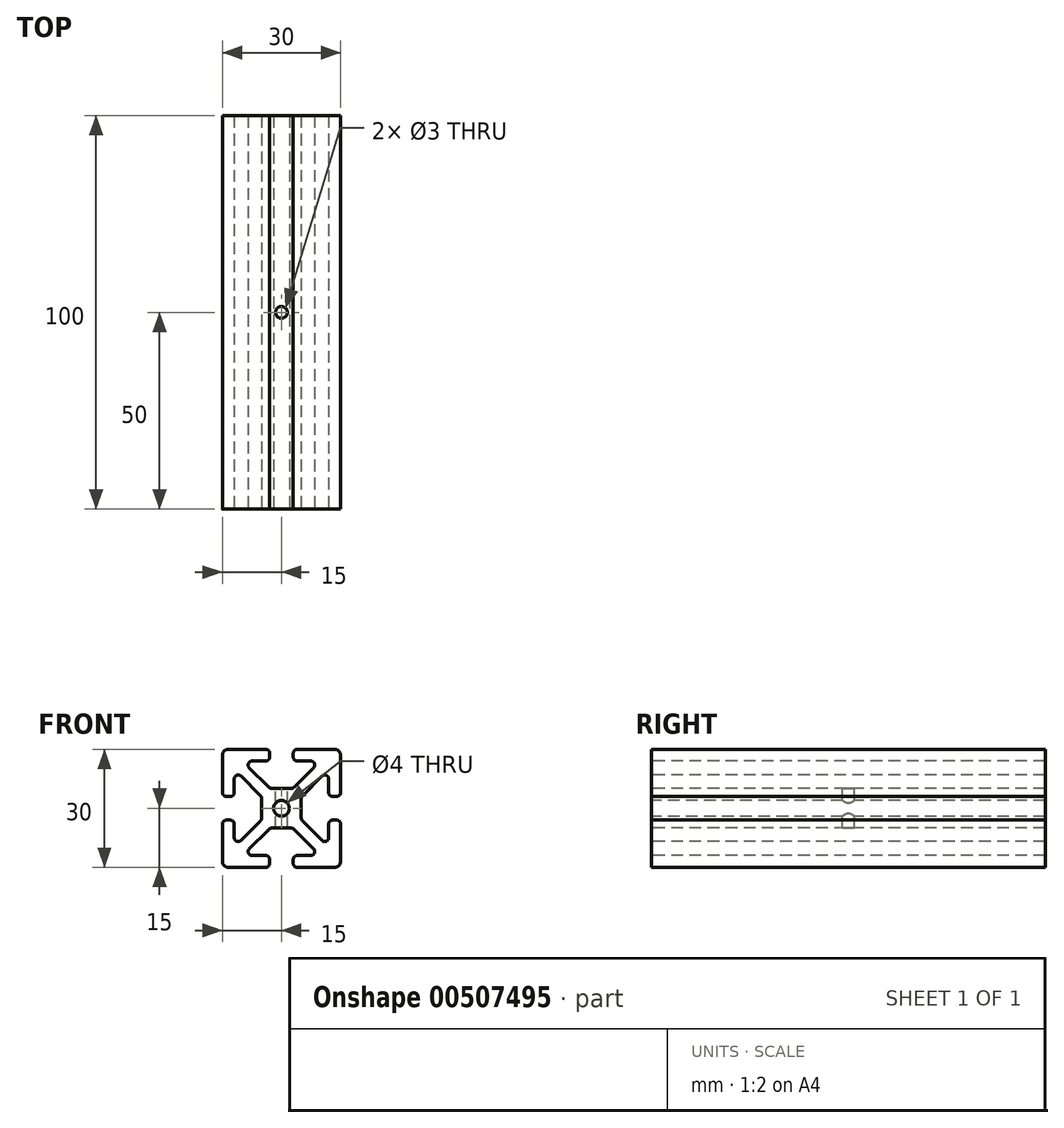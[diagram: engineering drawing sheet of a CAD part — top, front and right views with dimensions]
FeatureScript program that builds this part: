
annotation { "Feature Type Name" : "Feature", "Feature Type Description" : "" }
export const myFeature = defineFeature(function(context is Context, id is Id, definition is map)
    precondition{}
    {
        {
            var Q0;
            Q0=qCreatedBy(makeId("Front.planeOp"),FACE);
            var sketch = newSketch(context, id + "F0", { "sketchPlane" : qUnion([Q0])});
            skLineSegment(sketch, "E0.bottom", {"start": v(13.5, 15) * mm, "end": v(4, 15) * mm});
            skLineSegment(sketch, "E0.top", {"start": v(13.5, -15) * mm, "end": v(4, -15) * mm});
            skLineSegment(sketch, "E0.left", {"start": v(15, 13.5) * mm, "end": v(15, 4) * mm});
            skLineSegment(sketch, "E0.right", {"start": v(-15, 13.5) * mm, "end": v(-15, 4) * mm});
            skPoint(sketch, "E0.middle", {"position": v(0, 0) * mm});
            skLineSegment(sketch, "E1.bottom", {"start": v(7.46, 12) * mm, "end": v(4, 12) * mm});
            skLineSegment(sketch, "E1.top", {"start": v(7.46, -12) * mm, "end": v(4, -12) * mm});
            skLineSegment(sketch, "E1.left", {"start": v(12, 7.46) * mm, "end": v(12, 4) * mm});
            skLineSegment(sketch, "E1.right", {"start": v(-12, 7.46) * mm, "end": v(-12, 4) * mm});
            skLineSegment(sketch, "E2", {"start": v(8.17, 10.3) * mm, "end": v(3.32, 5.44) * mm});
            skLineSegment(sketch, "E3", {"start": v(-8.17, -10.3) * mm, "end": v(-3.32, -5.44) * mm});
            skLineSegment(sketch, "E4", {"start": v(-8.17, 10.3) * mm, "end": v(-3.32, 5.44) * mm});
            skLineSegment(sketch, "E5", {"start": v(-10.3, 8.17) * mm, "end": v(-5.44, 3.32) * mm});
            skPoint(sketch, "E6.orphan", {"position": v(12, 12) * mm});
            skPoint(sketch, "E7.orphan", {"position": v(12, -12) * mm});
            skPoint(sketch, "E8.orphan", {"position": v(-12, -12) * mm});
            skPoint(sketch, "E9.orphan", {"position": v(-12, 12) * mm});
            skLineSegment(sketch, "E10.trimOffspring", {"start": v(-5.44, -3.32) * mm, "end": v(-10.3, -8.17) * mm});
            skLineSegment(sketch, "E11.trimOffspring", {"start": v(5.44, -3.32) * mm, "end": v(10.3, -8.17) * mm});
            skLineSegment(sketch, "E12.trimOffspring", {"start": v(5.44, 3.32) * mm, "end": v(10.3, 8.17) * mm});
            skLineSegment(sketch, "E13.trimOffspring", {"start": v(3.32, -5.44) * mm, "end": v(8.17, -10.3) * mm});
            skLineSegment(sketch, "E14.bottom", {"start": v(2.26, 5) * mm, "end": v(-2.26, 5) * mm});
            skLineSegment(sketch, "E14.top", {"start": v(2.26, -5) * mm, "end": v(-2.26, -5) * mm});
            skLineSegment(sketch, "E14.left", {"start": v(5, 2.26) * mm, "end": v(5, -2.26) * mm});
            skLineSegment(sketch, "E14.right", {"start": v(-5, 2.26) * mm, "end": v(-5, -2.26) * mm});
            skPoint(sketch, "E15.orphan", {"position": v(5, 5) * mm});
            skPoint(sketch, "E16.orphan", {"position": v(5, -5) * mm});
            skPoint(sketch, "E17.orphan", {"position": v(-5, -5) * mm});
            skPoint(sketch, "E18.orphan", {"position": v(-5, 5) * mm});
            skCircle(sketch, "E19", {"center": v(0, 0) * mm, "radius": 2 * mm});
            skLineSegment(sketch, "E20", {"start": v(-3, 14) * mm, "end": v(-3, 13) * mm});
            skLineSegment(sketch, "E21", {"start": v(3, 14) * mm, "end": v(3, 13) * mm});
            skLineSegment(sketch, "E22.trimOffspring", {"start": v(-3, -13) * mm, "end": v(-3, -14) * mm});
            skLineSegment(sketch, "E23.trimOffspring", {"start": v(-4, 12) * mm, "end": v(-7.46, 12) * mm});
            skLineSegment(sketch, "E24.trimOffspring", {"start": v(-4, 15) * mm, "end": v(-13.5, 15) * mm});
            skLineSegment(sketch, "E25.trimOffspring", {"start": v(3, -13) * mm, "end": v(3, -14) * mm});
            skLineSegment(sketch, "E26.trimOffspring", {"start": v(-4, -12) * mm, "end": v(-7.46, -12) * mm});
            skLineSegment(sketch, "E27.trimOffspring", {"start": v(-4, -15) * mm, "end": v(-13.5, -15) * mm});
            skLineSegment(sketch, "E28", {"start": v(-14, 3) * mm, "end": v(-13, 3) * mm});
            skLineSegment(sketch, "E29", {"start": v(-14, -3) * mm, "end": v(-13, -3) * mm});
            skLineSegment(sketch, "E30.trimOffspring", {"start": v(-12, -4) * mm, "end": v(-12, -7.46) * mm});
            skLineSegment(sketch, "E31.trimOffspring", {"start": v(-15, -4) * mm, "end": v(-15, -13.5) * mm});
            skLineSegment(sketch, "E32.trimOffspring", {"start": v(13, 3) * mm, "end": v(14, 3) * mm});
            skLineSegment(sketch, "E33.trimOffspring", {"start": v(13, -3) * mm, "end": v(14, -3) * mm});
            skLineSegment(sketch, "E34.trimOffspring", {"start": v(12, -4) * mm, "end": v(12, -7.46) * mm});
            skLineSegment(sketch, "E35.trimOffspring", {"start": v(15, -4) * mm, "end": v(15, -13.5) * mm});
            skPoint(sketch, "E36.visualSharp", {"position": v(-15, 15) * mm});
            skArc(sketch, "E36.filletArc", {"start": v(-13.5, 15) * mm, "mid": v(-14.56, 14.56) * mm, "end": v(-15, 13.5) * mm});
            skPoint(sketch, "E37.visualSharp", {"position": v(15, 15) * mm});
            skArc(sketch, "E37.filletArc", {"start": v(15, 13.5) * mm, "mid": v(14.56, 14.56) * mm, "end": v(13.5, 15) * mm});
            skPoint(sketch, "E38.visualSharp", {"position": v(15, -15) * mm});
            skArc(sketch, "E38.filletArc", {"start": v(13.5, -15) * mm, "mid": v(14.56, -14.56) * mm, "end": v(15, -13.5) * mm});
            skPoint(sketch, "E39.visualSharp", {"position": v(-15, -15) * mm});
            skArc(sketch, "E39.filletArc", {"start": v(-15, -13.5) * mm, "mid": v(-14.56, -14.56) * mm, "end": v(-13.5, -15) * mm});
            skPoint(sketch, "E40.visualSharp", {"position": v(-5, -2.88) * mm});
            skArc(sketch, "E40.filletArc", {"start": v(-5.44, -3.32) * mm, "mid": v(-5.11, -2.83) * mm, "end": v(-5, -2.26) * mm});
            skPoint(sketch, "E41.visualSharp", {"position": v(-2.88, -5) * mm});
            skArc(sketch, "E41.filletArc", {"start": v(-2.26, -5) * mm, "mid": v(-2.83, -5.11) * mm, "end": v(-3.32, -5.44) * mm});
            skPoint(sketch, "E42.visualSharp", {"position": v(2.88, -5) * mm});
            skArc(sketch, "E42.filletArc", {"start": v(3.32, -5.44) * mm, "mid": v(2.83, -5.11) * mm, "end": v(2.26, -5) * mm});
            skPoint(sketch, "E43.visualSharp", {"position": v(5, -2.88) * mm});
            skArc(sketch, "E43.filletArc", {"start": v(5, -2.26) * mm, "mid": v(5.11, -2.83) * mm, "end": v(5.44, -3.32) * mm});
            skPoint(sketch, "E44.visualSharp", {"position": v(5, 2.88) * mm});
            skArc(sketch, "E44.filletArc", {"start": v(5.44, 3.32) * mm, "mid": v(5.11, 2.83) * mm, "end": v(5, 2.26) * mm});
            skPoint(sketch, "E45.visualSharp", {"position": v(2.88, 5) * mm});
            skArc(sketch, "E45.filletArc", {"start": v(2.26, 5) * mm, "mid": v(2.83, 5.11) * mm, "end": v(3.32, 5.44) * mm});
            skPoint(sketch, "E46.visualSharp", {"position": v(-2.88, 5) * mm});
            skArc(sketch, "E46.filletArc", {"start": v(-3.32, 5.44) * mm, "mid": v(-2.83, 5.11) * mm, "end": v(-2.26, 5) * mm});
            skPoint(sketch, "E47.visualSharp", {"position": v(-3, 12) * mm});
            skArc(sketch, "E47.filletArc", {"start": v(-4, 12) * mm, "mid": v(-3.3, 12.3) * mm, "end": v(-3, 13) * mm});
            skPoint(sketch, "E48.visualSharp", {"position": v(-3, 15) * mm});
            skArc(sketch, "E48.filletArc", {"start": v(-3, 14) * mm, "mid": v(-3.3, 14.7) * mm, "end": v(-4, 15) * mm});
            skPoint(sketch, "E49.visualSharp", {"position": v(3, 15) * mm});
            skArc(sketch, "E49.filletArc", {"start": v(4, 15) * mm, "mid": v(3.3, 14.7) * mm, "end": v(3, 14) * mm});
            skPoint(sketch, "E50.visualSharp", {"position": v(3, 12) * mm});
            skArc(sketch, "E50.filletArc", {"start": v(3, 13) * mm, "mid": v(3.3, 12.3) * mm, "end": v(4, 12) * mm});
            skPoint(sketch, "E51.visualSharp", {"position": v(12, 3) * mm});
            skArc(sketch, "E51.filletArc", {"start": v(12, 4) * mm, "mid": v(12.3, 3.3) * mm, "end": v(13, 3) * mm});
            skPoint(sketch, "E52.visualSharp", {"position": v(15, 3) * mm});
            skArc(sketch, "E52.filletArc", {"start": v(14, 3) * mm, "mid": v(14.7, 3.3) * mm, "end": v(15, 4) * mm});
            skPoint(sketch, "E53.visualSharp", {"position": v(15, -3) * mm});
            skArc(sketch, "E53.filletArc", {"start": v(15, -4) * mm, "mid": v(14.7, -3.3) * mm, "end": v(14, -3) * mm});
            skPoint(sketch, "E54.visualSharp", {"position": v(12, -3) * mm});
            skArc(sketch, "E54.filletArc", {"start": v(13, -3) * mm, "mid": v(12.3, -3.3) * mm, "end": v(12, -4) * mm});
            skPoint(sketch, "E55.visualSharp", {"position": v(3, -12) * mm});
            skArc(sketch, "E55.filletArc", {"start": v(4, -12) * mm, "mid": v(3.3, -12.3) * mm, "end": v(3, -13) * mm});
            skPoint(sketch, "E56.visualSharp", {"position": v(3, -15) * mm});
            skArc(sketch, "E56.filletArc", {"start": v(3, -14) * mm, "mid": v(3.3, -14.7) * mm, "end": v(4, -15) * mm});
            skPoint(sketch, "E57.visualSharp", {"position": v(-3, -12) * mm});
            skArc(sketch, "E57.filletArc", {"start": v(-3, -13) * mm, "mid": v(-3.3, -12.3) * mm, "end": v(-4, -12) * mm});
            skPoint(sketch, "E58.visualSharp", {"position": v(-3, -15) * mm});
            skArc(sketch, "E58.filletArc", {"start": v(-4, -15) * mm, "mid": v(-3.3, -14.7) * mm, "end": v(-3, -14) * mm});
            skPoint(sketch, "E59.visualSharp", {"position": v(-12, -3) * mm});
            skArc(sketch, "E59.filletArc", {"start": v(-12, -4) * mm, "mid": v(-12.3, -3.3) * mm, "end": v(-13, -3) * mm});
            skPoint(sketch, "E60.visualSharp", {"position": v(-15, -3) * mm});
            skArc(sketch, "E60.filletArc", {"start": v(-14, -3) * mm, "mid": v(-14.7, -3.3) * mm, "end": v(-15, -4) * mm});
            skPoint(sketch, "E61.visualSharp", {"position": v(-15, 3) * mm});
            skArc(sketch, "E61.filletArc", {"start": v(-15, 4) * mm, "mid": v(-14.7, 3.3) * mm, "end": v(-14, 3) * mm});
            skPoint(sketch, "E62.visualSharp", {"position": v(-12, 3) * mm});
            skArc(sketch, "E62.filletArc", {"start": v(-13, 3) * mm, "mid": v(-12.3, 3.3) * mm, "end": v(-12, 4) * mm});
            skPoint(sketch, "E63.visualSharp", {"position": v(9.88, 12) * mm});
            skArc(sketch, "E63.filletArc", {"start": v(8.17, 10.3) * mm, "mid": v(8.39, 11.38) * mm, "end": v(7.46, 12) * mm});
            skPoint(sketch, "E64.visualSharp", {"position": v(12, 9.88) * mm});
            skArc(sketch, "E64.filletArc", {"start": v(12, 7.46) * mm, "mid": v(11.38, 8.39) * mm, "end": v(10.3, 8.17) * mm});
            skPoint(sketch, "E65.visualSharp", {"position": v(12, -9.88) * mm});
            skArc(sketch, "E65.filletArc", {"start": v(10.3, -8.17) * mm, "mid": v(11.38, -8.39) * mm, "end": v(12, -7.46) * mm});
            skPoint(sketch, "E66.visualSharp", {"position": v(9.88, -12) * mm});
            skArc(sketch, "E66.filletArc", {"start": v(7.46, -12) * mm, "mid": v(8.39, -11.38) * mm, "end": v(8.17, -10.3) * mm});
            skPoint(sketch, "E67.visualSharp", {"position": v(-12, -9.88) * mm});
            skArc(sketch, "E67.filletArc", {"start": v(-12, -7.46) * mm, "mid": v(-11.38, -8.39) * mm, "end": v(-10.3, -8.17) * mm});
            skPoint(sketch, "E68.visualSharp", {"position": v(-9.88, -12) * mm});
            skArc(sketch, "E68.filletArc", {"start": v(-8.17, -10.3) * mm, "mid": v(-8.39, -11.38) * mm, "end": v(-7.46, -12) * mm});
            skPoint(sketch, "E69.visualSharp", {"position": v(-12, 9.88) * mm});
            skArc(sketch, "E69.filletArc", {"start": v(-10.3, 8.17) * mm, "mid": v(-11.38, 8.39) * mm, "end": v(-12, 7.46) * mm});
            skPoint(sketch, "E70.visualSharp", {"position": v(-9.88, 12) * mm});
            skArc(sketch, "E70.filletArc", {"start": v(-7.46, 12) * mm, "mid": v(-8.39, 11.38) * mm, "end": v(-8.17, 10.3) * mm});
            skPoint(sketch, "E71.visualSharp", {"position": v(-5, 2.88) * mm});
            skArc(sketch, "E71.filletArc", {"start": v(-5, 2.26) * mm, "mid": v(-5.11, 2.83) * mm, "end": v(-5.44, 3.32) * mm});
            skSolve(sketch);
        }
        {
            var Q0;
            Q0=qSketchRegion(id+"F0",true);
            extrude(context, id + "F1", {"entities" : qUnion([Q0]), "oppositeDirection" : true, "depth" : 100 * mm});
        }
        {
            var Q0;
            Q0=makeQuery(id+"F1.opExtrude","SWEPT_FACE",FACE,{"disambiguationData":[OSD([sQuery(id+"F0.wireOp",EDGE,"E14.bottom")])]});
            var sketch = newSketch(context, id + "F2", { "sketchPlane" : qUnion([Q0])});
            skCircle(sketch, "E72", {"center": v(0, 50) * mm, "radius": 1.5 * mm});
            skPoint(sketch, "E72.centerSnap0", {"position": v(0, 100) * mm});
            skPoint(sketch, "E72.centerSnap1", {"position": v(2.26, 50) * mm});
            skSolve(sketch);
        }
        {
            var Q0;
            Q0=qSketchRegion(id+"F2",true);
            extrude(context, id + "F3", {"entities" : qUnion([Q0]), "operationType" : NewBodyOperationType.REMOVE, "oppositeDirection" : true, "depth" : 10 * mm});
        }
    });
